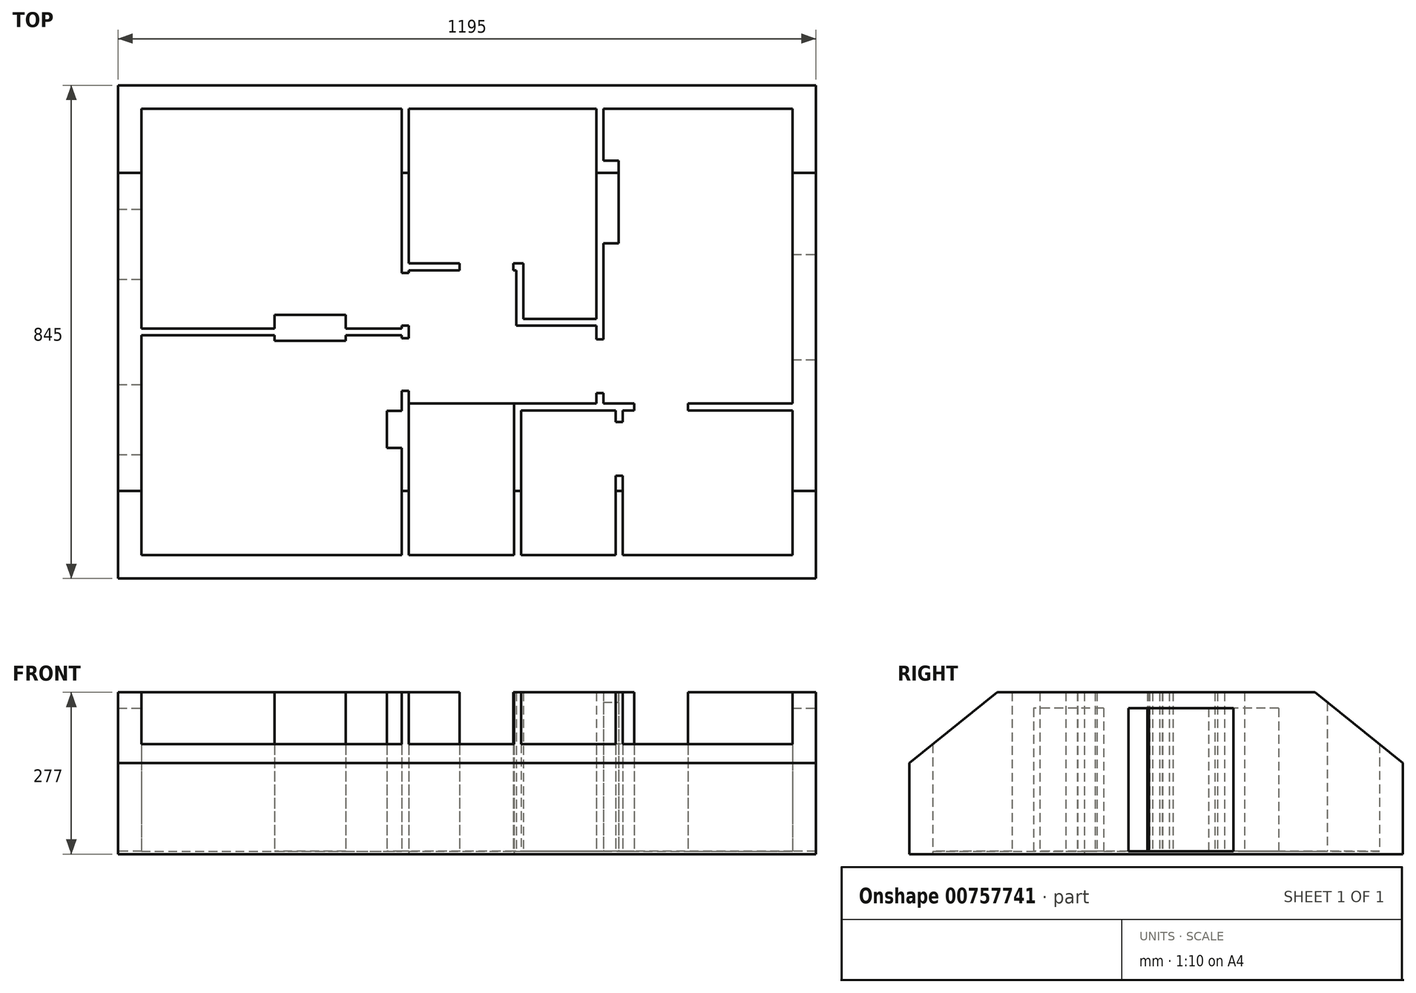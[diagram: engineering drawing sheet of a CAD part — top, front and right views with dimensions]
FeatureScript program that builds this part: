
annotation { "Feature Type Name" : "Feature", "Feature Type Description" : "" }
export const myFeature = defineFeature(function(context is Context, id is Id, definition is map)
    precondition{}
    {
        {
            var Q0;
            Q0=qCreatedBy(makeId("Top.planeOp"),FACE);
            var sketch = newSketch(context, id + "F0", { "sketchPlane" : qUnion([Q0])});
            skLineSegment(sketch, "E0", {"start": v(0, 0) * mm, "end": v(1145, 0) * mm, "construction": true});
            skLineSegment(sketch, "E1", {"start": v(1145, 0) * mm, "end": v(1145, 795) * mm, "construction": true});
            skLineSegment(sketch, "E2", {"start": v(1145, 795) * mm, "end": v(0, 795) * mm, "construction": true});
            skLineSegment(sketch, "E3", {"start": v(0, 795) * mm, "end": v(0, 0) * mm, "construction": true});
            skLineSegment(sketch, "E4", {"start": v(800, 0) * mm, "end": v(800, 15) * mm, "construction": true});
            skLineSegment(sketch, "E5", {"start": v(800, 397.5) * mm, "end": v(0, 397.5) * mm, "construction": true});
            skLineSegment(sketch, "E6.0", {"start": v(1170, 820) * mm, "end": v(-25, 820) * mm});
            skLineSegment(sketch, "E6.1", {"start": v(1170, -25) * mm, "end": v(1170, 820) * mm});
            skLineSegment(sketch, "E6.2", {"start": v(-25, -25) * mm, "end": v(1170, -25) * mm});
            skLineSegment(sketch, "E6.3", {"start": v(-25, 820) * mm, "end": v(-25, -25) * mm});
            skLineSegment(sketch, "E7.0", {"start": v(1130, 780) * mm, "end": v(15, 780) * mm});
            skLineSegment(sketch, "E7.1", {"start": v(1130, 15) * mm, "end": v(1130, 780) * mm});
            skLineSegment(sketch, "E7.2", {"start": v(15, 15) * mm, "end": v(1130, 15) * mm});
            skLineSegment(sketch, "E7.3", {"start": v(15, 780) * mm, "end": v(15, 15) * mm});
            skLineSegment(sketch, "E8.0", {"start": v(806, 263) * mm, "end": v(806, 795) * mm});
            skLineSegment(sketch, "E9.0", {"start": v(794, 263) * mm, "end": v(794, 795) * mm});
            skLineSegment(sketch, "E10", {"start": v(461, 386.5) * mm, "end": v(461, 262.5) * mm});
            skLineSegment(sketch, "E11", {"start": v(461, 262.5) * mm, "end": v(435, 262.5) * mm});
            skLineSegment(sketch, "E12", {"start": v(435, 262.5) * mm, "end": v(435, 198.5) * mm});
            skLineSegment(sketch, "E13", {"start": v(435, 198.5) * mm, "end": v(461, 198.5) * mm});
            skLineSegment(sketch, "E14", {"start": v(461, 198.5) * mm, "end": v(461, 15) * mm});
            skLineSegment(sketch, "E15", {"start": v(806, 691) * mm, "end": v(832, 691) * mm});
            skLineSegment(sketch, "E16", {"start": v(832, 691) * mm, "end": v(832, 549) * mm});
            skLineSegment(sketch, "E17", {"start": v(832, 549) * mm, "end": v(806, 549) * mm});
            skLineSegment(sketch, "E18", {"start": v(365, 426.5) * mm, "end": v(243, 426.5) * mm});
            skLineSegment(sketch, "E19", {"start": v(323, 15) * mm, "end": v(323, -25) * mm});
            skLineSegment(sketch, "E20", {"start": v(461, 15) * mm, "end": v(461, -25) * mm});
            skLineSegment(sketch, "E21", {"start": v(1130, 530) * mm, "end": v(1170, 530) * mm});
            skLineSegment(sketch, "E22", {"start": v(1130, 350) * mm, "end": v(1170, 350) * mm});
            skPoint(sketch, "E23.orphan", {"position": v(238, -25) * mm});
            skPoint(sketch, "E24.end.orphan", {"position": v(88, -25) * mm});
            skLineSegment(sketch, "E25", {"start": v(-25, 487.5) * mm, "end": v(15, 487.5) * mm});
            skLineSegment(sketch, "E26", {"start": v(-25, 607.5) * mm, "end": v(15, 607.5) * mm});
            skLineSegment(sketch, "E27", {"start": v(-25, 307.5) * mm, "end": v(15, 307.5) * mm});
            skLineSegment(sketch, "E28", {"start": v(-25, 187.5) * mm, "end": v(15, 187.5) * mm});
            skLineSegment(sketch, "E29", {"start": v(794, 408) * mm, "end": v(657, 408) * mm});
            skLineSegment(sketch, "E30", {"start": v(657, 408) * mm, "end": v(657, 503) * mm});
            skLineSegment(sketch, "E31", {"start": v(657, 503) * mm, "end": v(473, 503) * mm});
            skLineSegment(sketch, "E32.0", {"start": v(669, 515) * mm, "end": v(473, 515) * mm});
            skLineSegment(sketch, "E32.1", {"start": v(669, 420) * mm, "end": v(669, 515) * mm});
            skLineSegment(sketch, "E32.2", {"start": v(794, 420) * mm, "end": v(669, 420) * mm});
            skLineSegment(sketch, "E33", {"start": v(652, 515) * mm, "end": v(652, 503) * mm});
            skLineSegment(sketch, "E34", {"start": v(560, 515) * mm, "end": v(560, 503) * mm});
            skLineSegment(sketch, "E35", {"start": v(461, 403.5) * mm, "end": v(365, 403.5) * mm});
            skLineSegment(sketch, "E36", {"start": v(365, 403.5) * mm, "end": v(15, 403.5) * mm});
            skLineSegment(sketch, "E37", {"start": v(15, 403.5) * mm, "end": v(15, 382.16) * mm});
            skLineSegment(sketch, "E38", {"start": v(794, 385) * mm, "end": v(806, 385) * mm});
            skLineSegment(sketch, "E39", {"start": v(806, 385) * mm, "end": v(806, 293) * mm});
            skLineSegment(sketch, "E40", {"start": v(806, 293) * mm, "end": v(794, 293) * mm});
            skLineSegment(sketch, "E41.MirrorCS", {"start": v(461, 391.5) * mm, "end": v(365, 391.5) * mm});
            skLineSegment(sketch, "E42.MirrorCS", {"start": v(365, 391.5) * mm, "end": v(15, 391.5) * mm});
            skLineSegment(sketch, "E43", {"start": v(461, 403.5) * mm, "end": v(461, 408.5) * mm});
            skLineSegment(sketch, "E44", {"start": v(461, 408.5) * mm, "end": v(473, 408.5) * mm});
            skLineSegment(sketch, "E45", {"start": v(473, 408.5) * mm, "end": v(473, 386.5) * mm});
            skLineSegment(sketch, "E46", {"start": v(473, 386.5) * mm, "end": v(461, 386.5) * mm});
            skLineSegment(sketch, "E47", {"start": v(461, 386.5) * mm, "end": v(461, 391.5) * mm});
            skLineSegment(sketch, "E48", {"start": v(243, 426.5) * mm, "end": v(243, 382.5) * mm});
            skLineSegment(sketch, "E49", {"start": v(243, 382.5) * mm, "end": v(364.87, 382.5) * mm});
            skLineSegment(sketch, "E50", {"start": v(364.87, 382.5) * mm, "end": v(365, 426.5) * mm});
            skLineSegment(sketch, "E51", {"start": v(461, 408.5) * mm, "end": v(461, 780) * mm});
            skLineSegment(sketch, "E52", {"start": v(461, 780) * mm, "end": v(473, 780) * mm});
            skLineSegment(sketch, "E53", {"start": v(473, 780) * mm, "end": v(473, 408.5) * mm});
            skLineSegment(sketch, "E54", {"start": v(461, 498.5) * mm, "end": v(473, 498.5) * mm});
            skLineSegment(sketch, "E55", {"start": v(473, 386.5) * mm, "end": v(473, 15) * mm});
            skLineSegment(sketch, "E56", {"start": v(461, 296.5) * mm, "end": v(473, 296.5) * mm});
            skLineSegment(sketch, "E57", {"start": v(653, 15) * mm, "end": v(653, 275) * mm});
            skLineSegment(sketch, "E58", {"start": v(653, 275) * mm, "end": v(670, 275) * mm});
            skLineSegment(sketch, "E59", {"start": v(665, 263) * mm, "end": v(665, 15) * mm});
            skLineSegment(sketch, "E60", {"start": v(653, 275) * mm, "end": v(473, 275) * mm});
            skLineSegment(sketch, "E61", {"start": v(670, 275) * mm, "end": v(794, 275) * mm});
            skLineSegment(sketch, "E62", {"start": v(794, 275) * mm, "end": v(794, 263) * mm});
            skLineSegment(sketch, "E63", {"start": v(665, 263) * mm, "end": v(794, 263) * mm});
            skLineSegment(sketch, "E64", {"start": v(794, 275) * mm, "end": v(839, 275) * mm});
            skLineSegment(sketch, "E65", {"start": v(839, 275) * mm, "end": v(839, 15) * mm});
            skLineSegment(sketch, "E66", {"start": v(839, 15) * mm, "end": v(827, 15) * mm});
            skLineSegment(sketch, "E67", {"start": v(827, 15) * mm, "end": v(827, 263) * mm});
            skLineSegment(sketch, "E68", {"start": v(827, 263) * mm, "end": v(794, 263) * mm});
            skLineSegment(sketch, "E69", {"start": v(839, 275) * mm, "end": v(1130, 275) * mm});
            skLineSegment(sketch, "E70", {"start": v(1130, 275) * mm, "end": v(1130, 263) * mm});
            skLineSegment(sketch, "E71", {"start": v(1130, 263) * mm, "end": v(827, 263) * mm});
            skLineSegment(sketch, "E72.trimOffspring", {"start": v(800, 263) * mm, "end": v(800, 795) * mm, "construction": true});
            skLineSegment(sketch, "E73", {"start": v(827, 243) * mm, "end": v(839, 243) * mm});
            skLineSegment(sketch, "E74", {"start": v(839, 243) * mm, "end": v(839, 151) * mm});
            skLineSegment(sketch, "E75", {"start": v(839, 151) * mm, "end": v(827, 151) * mm});
            skLineSegment(sketch, "E76", {"start": v(859, 275) * mm, "end": v(859, 263) * mm});
            skLineSegment(sketch, "E77", {"start": v(859, 263) * mm, "end": v(951, 263) * mm});
            skLineSegment(sketch, "E78", {"start": v(951, 263) * mm, "end": v(951, 275) * mm});
            skSolve(sketch);
        }
        {
            var Q0;
            {var subQ5=sQuery(id+"F0.wireOp",EDGE,"E78");Q0=makeQuery(id+"F0.imprint","IMPRINT",FACE,{"disambiguationData":[TD([[makeQuery(id+"F0.imprint","IMPRINT",EDGE,{"derivedFrom":subQ5}),-1.0]])]});}
            var Q1;
            {var subQ3=sQuery(id+"F0.wireOp",EDGE,"E29");Q1=makeQuery(id+"F0.imprint","IMPRINT",FACE,{"disambiguationData":[TD([[makeQuery(id+"F0.imprint","IMPRINT",EDGE,{"derivedFrom":subQ3}),-1.0]])]});}
            var Q2;
            {var subQ2=sQuery(id+"F0.wireOp",EDGE,"E19");Q2=makeQuery(id+"F0.imprint","IMPRINT",FACE,{"disambiguationData":[TD([[makeQuery(id+"F0.imprint","IMPRINT",EDGE,{"derivedFrom":subQ2}),1.0]])]});}
            var Q3;
            {var subQ0=sQuery(id+"F0.wireOp",EDGE,"E15");Q3=makeQuery(id+"F0.imprint","IMPRINT",FACE,{"disambiguationData":[TD([[makeQuery(id+"F0.imprint","IMPRINT",EDGE,{"derivedFrom":subQ0}),1.0]])]});}
            var Q4;
            {var subQ0=sQuery(id+"F0.wireOp",EDGE,"E25");Q4=makeQuery(id+"F0.imprint","IMPRINT",FACE,{"disambiguationData":[TD([[makeQuery(id+"F0.imprint","IMPRINT",EDGE,{"derivedFrom":subQ0}),1.0]])]});}
            var Q5;
            {var subQ0=sQuery(id+"F0.wireOp",EDGE,"E27");Q5=makeQuery(id+"F0.imprint","IMPRINT",FACE,{"disambiguationData":[TD([[makeQuery(id+"F0.imprint","IMPRINT",EDGE,{"derivedFrom":subQ0}),-1.0]])]});}
            var Q6;
            {var subQ5=sQuery(id+"F0.wireOp",EDGE,"E25");Q6=makeQuery(id+"F0.imprint","IMPRINT",FACE,{"disambiguationData":[TD([[makeQuery(id+"F0.imprint","IMPRINT",EDGE,{"derivedFrom":subQ5}),-1.0]])]});}
            var Q7;
            {var subQ4=sQuery(id+"F0.wireOp",EDGE,"E19");Q7=makeQuery(id+"F0.imprint","IMPRINT",FACE,{"disambiguationData":[TD([[makeQuery(id+"F0.imprint","IMPRINT",EDGE,{"derivedFrom":subQ4}),-1.0]])]});}
            var Q8;
            {var subQ4=sQuery(id+"F0.wireOp",EDGE,"E7.1");var subQ7=sQuery(id+"F0.wireOp",EDGE,"E71");var subQ8=makeQuery(id+"F0.imprint","INTERSECT",VERTEX,{"derivedFrom":[subQ4,subQ7]});Q8=makeQuery(id+"F0.imprint","IMPRINT",FACE,{"disambiguationData":[TD([[makeQuery(id+"F0.imprint","IMPRINT",EDGE,{"disambiguationData":[TD([[subQ8,1.0]])],"derivedFrom":subQ4}),1.0]])]});}
            var Q9;
            {var subQ2=sQuery(id+"F0.wireOp",EDGE,"E76");Q9=makeQuery(id+"F0.imprint","IMPRINT",FACE,{"disambiguationData":[TD([[makeQuery(id+"F0.imprint","IMPRINT",EDGE,{"derivedFrom":subQ2}),1.0]])]});}
            var Q10;
            {var subQ5=sQuery(id+"F0.wireOp",EDGE,"E49");Q10=makeQuery(id+"F0.imprint","IMPRINT",FACE,{"disambiguationData":[TD([[makeQuery(id+"F0.imprint","IMPRINT",EDGE,{"derivedFrom":subQ5}),1.0]])]});}
            var Q11;
            {var subQ6=sQuery(id+"F0.wireOp",EDGE,"E54");Q11=makeQuery(id+"F0.imprint","IMPRINT",FACE,{"disambiguationData":[TD([[makeQuery(id+"F0.imprint","IMPRINT",EDGE,{"derivedFrom":subQ6}),1.0]])]});}
            var Q12;
            {var subQ0=sQuery(id+"F0.wireOp",EDGE,"E44");Q12=makeQuery(id+"F0.imprint","IMPRINT",FACE,{"disambiguationData":[TD([[makeQuery(id+"F0.imprint","IMPRINT",EDGE,{"derivedFrom":subQ0}),1.0]])]});}
            var Q13;
            {var subQ0=sQuery(id+"F0.wireOp",EDGE,"E18");Q13=makeQuery(id+"F0.imprint","IMPRINT",FACE,{"disambiguationData":[TD([[makeQuery(id+"F0.imprint","IMPRINT",EDGE,{"derivedFrom":subQ0}),1.0]])]});}
            var Q14;
            {var subQ9=sQuery(id+"F0.wireOp",EDGE,"E29");Q14=makeQuery(id+"F0.imprint","IMPRINT",FACE,{"disambiguationData":[TD([[makeQuery(id+"F0.imprint","IMPRINT",EDGE,{"derivedFrom":subQ9}),1.0]])]});}
            var Q15;
            {var subQ0=sQuery(id+"F0.wireOp",EDGE,"E21");Q15=makeQuery(id+"F0.imprint","IMPRINT",FACE,{"disambiguationData":[TD([[makeQuery(id+"F0.imprint","IMPRINT",EDGE,{"derivedFrom":subQ0}),-1.0]])]});}
            var Q16;
            {var subQ7=sQuery(id+"F0.wireOp",EDGE,"E59");Q16=makeQuery(id+"F0.imprint","IMPRINT",FACE,{"disambiguationData":[TD([[makeQuery(id+"F0.imprint","IMPRINT",EDGE,{"derivedFrom":subQ7}),1.0]])]});}
            var Q17;
            {var subQ0=sQuery(id+"F0.wireOp",EDGE,"E34");Q17=makeQuery(id+"F0.imprint","IMPRINT",FACE,{"disambiguationData":[TD([[makeQuery(id+"F0.imprint","IMPRINT",EDGE,{"derivedFrom":subQ0}),-1.0]])]});}
            var Q18;
            {var subQ0=sQuery(id+"F0.wireOp",EDGE,"E46");Q18=makeQuery(id+"F0.imprint","IMPRINT",FACE,{"disambiguationData":[TD([[makeQuery(id+"F0.imprint","IMPRINT",EDGE,{"derivedFrom":subQ0}),1.0]])]});}
            var Q19;
            {var subQ0=sQuery(id+"F0.wireOp",EDGE,"E11");Q19=makeQuery(id+"F0.imprint","IMPRINT",FACE,{"disambiguationData":[TD([[makeQuery(id+"F0.imprint","IMPRINT",EDGE,{"derivedFrom":subQ0}),-1.0]])]});}
            var Q20;
            {var subQ5=sQuery(id+"F0.wireOp",EDGE,"E6.0");Q20=makeQuery(id+"F0.imprint","IMPRINT",FACE,{"disambiguationData":[TD([[makeQuery(id+"F0.imprint","IMPRINT",EDGE,{"derivedFrom":subQ5}),1.0]])]});}
            var Q21;
            {var subQ2=sQuery(id+"F0.wireOp",EDGE,"E73");Q21=makeQuery(id+"F0.imprint","IMPRINT",FACE,{"disambiguationData":[TD([[makeQuery(id+"F0.imprint","IMPRINT",EDGE,{"derivedFrom":subQ2}),-1.0]])]});}
            var Q22;
            {var subQ0=sQuery(id+"F0.wireOp",EDGE,"E11");Q22=makeQuery(id+"F0.imprint","IMPRINT",FACE,{"disambiguationData":[TD([[makeQuery(id+"F0.imprint","IMPRINT",EDGE,{"derivedFrom":subQ0}),1.0]])]});}
            var Q23;
            {var subQ10=sQuery(id+"F0.wireOp",EDGE,"E32.1");Q23=makeQuery(id+"F0.imprint","IMPRINT",FACE,{"disambiguationData":[TD([[makeQuery(id+"F0.imprint","IMPRINT",EDGE,{"derivedFrom":subQ10}),-1.0]])]});}
            var Q24;
            {var subQ0=sQuery(id+"F0.wireOp",EDGE,"E15");Q24=makeQuery(id+"F0.imprint","IMPRINT",FACE,{"disambiguationData":[TD([[makeQuery(id+"F0.imprint","IMPRINT",EDGE,{"derivedFrom":subQ0}),-1.0]])]});}
            var Q25;
            {var subQ0=sQuery(id+"F0.wireOp",EDGE,"E33");Q25=makeQuery(id+"F0.imprint","IMPRINT",FACE,{"disambiguationData":[TD([[makeQuery(id+"F0.imprint","IMPRINT",EDGE,{"derivedFrom":subQ0}),-1.0]])]});}
            var Q26;
            {var subQ5=sQuery(id+"F0.wireOp",EDGE,"E75");Q26=makeQuery(id+"F0.imprint","IMPRINT",FACE,{"disambiguationData":[TD([[makeQuery(id+"F0.imprint","IMPRINT",EDGE,{"derivedFrom":subQ5}),1.0]])]});}
            var Q27;
            {var subQ3=sQuery(id+"F0.wireOp",EDGE,"E57");Q27=makeQuery(id+"F0.imprint","IMPRINT",FACE,{"disambiguationData":[TD([[makeQuery(id+"F0.imprint","IMPRINT",EDGE,{"derivedFrom":subQ3}),-1.0]])]});}
            var Q28;
            {var subQ8=sQuery(id+"F0.wireOp",EDGE,"E20");Q28=makeQuery(id+"F0.imprint","IMPRINT",FACE,{"disambiguationData":[TD([[makeQuery(id+"F0.imprint","IMPRINT",EDGE,{"derivedFrom":subQ8}),1.0]])]});}
            var Q29;
            {var subQ0=sQuery(id+"F0.wireOp",EDGE,"E38");Q29=makeQuery(id+"F0.imprint","IMPRINT",FACE,{"disambiguationData":[TD([[makeQuery(id+"F0.imprint","IMPRINT",EDGE,{"derivedFrom":subQ0}),-1.0]])]});}
            var Q30;
            {var subQ0=sQuery(id+"F0.wireOp",EDGE,"E36");var subQ1=sQuery(id+"F0.wireOp",EDGE,"E7.3");var subQ2=makeQuery(id+"F0.imprint","INTERSECT",VERTEX,{"derivedFrom":[subQ1,subQ0]});Q30=makeQuery(id+"F0.imprint","IMPRINT",FACE,{"disambiguationData":[TD([[makeQuery(id+"F0.imprint","IMPRINT",EDGE,{"disambiguationData":[TD([[subQ2,-1.0]])],"derivedFrom":subQ1}),1.0]])]});}
            var Q31;
            {var subQ3=sQuery(id+"F0.wireOp",EDGE,"E40");Q31=makeQuery(id+"F0.imprint","IMPRINT",FACE,{"disambiguationData":[TD([[makeQuery(id+"F0.imprint","IMPRINT",EDGE,{"derivedFrom":subQ3}),1.0]])]});}
            var Q32;
            {var subQ5=sQuery(id+"F0.wireOp",EDGE,"E38");Q32=makeQuery(id+"F0.imprint","IMPRINT",FACE,{"disambiguationData":[TD([[makeQuery(id+"F0.imprint","IMPRINT",EDGE,{"derivedFrom":subQ5}),1.0]])]});}
            var Q33;
            {var subQ3=sQuery(id+"F0.wireOp",EDGE,"E73");Q33=makeQuery(id+"F0.imprint","IMPRINT",FACE,{"disambiguationData":[TD([[makeQuery(id+"F0.imprint","IMPRINT",EDGE,{"derivedFrom":subQ3}),1.0]])]});}
            var Q34;
            {var subQ3=sQuery(id+"F0.wireOp",EDGE,"E64");var subQ5=sQuery(id+"F0.wireOp",EDGE,"E8.0");var subQ6=makeQuery(id+"F0.imprint","INTERSECT",VERTEX,{"derivedFrom":[subQ5,subQ3]});Q34=makeQuery(id+"F0.imprint","IMPRINT",FACE,{"disambiguationData":[TD([[makeQuery(id+"F0.imprint","IMPRINT",EDGE,{"disambiguationData":[TD([[subQ6,1.0]])],"derivedFrom":subQ5}),-1.0]])]});}
            var Q35;
            {var subQ5=sQuery(id+"F0.wireOp",EDGE,"E76");Q35=makeQuery(id+"F0.imprint","IMPRINT",FACE,{"disambiguationData":[TD([[makeQuery(id+"F0.imprint","IMPRINT",EDGE,{"derivedFrom":subQ5}),-1.0]])]});}
            var Q36;
            {var subQ6=sQuery(id+"F0.wireOp",EDGE,"E35");Q36=makeQuery(id+"F0.imprint","IMPRINT",FACE,{"disambiguationData":[TD([[makeQuery(id+"F0.imprint","IMPRINT",EDGE,{"derivedFrom":subQ6}),1.0]])]});}
            var Q37;
            {var subQ0=sQuery(id+"F0.wireOp",EDGE,"E48");var subQ1=sQuery(id+"F0.wireOp",EDGE,"E36");var subQ2=makeQuery(id+"F0.imprint","INTERSECT",VERTEX,{"derivedFrom":[subQ1,subQ0]});Q37=makeQuery(id+"F0.imprint","IMPRINT",FACE,{"disambiguationData":[TD([[makeQuery(id+"F0.imprint","IMPRINT",EDGE,{"disambiguationData":[TD([[subQ2,1.0]])],"derivedFrom":subQ1}),1.0]])]});}
            var Q38;
            {var subQ0=sQuery(id+"F0.wireOp",EDGE,"E64");var subQ1=sQuery(id+"F0.wireOp",EDGE,"E8.0");var subQ2=makeQuery(id+"F0.imprint","INTERSECT",VERTEX,{"derivedFrom":[subQ1,subQ0]});Q38=makeQuery(id+"F0.imprint","IMPRINT",FACE,{"disambiguationData":[TD([[makeQuery(id+"F0.imprint","IMPRINT",EDGE,{"disambiguationData":[TD([[subQ2,1.0]])],"derivedFrom":subQ1}),1.0]])]});}
            var Q39;
            {var subQ1=sQuery(id+"F0.wireOp",EDGE,"E18");Q39=makeQuery(id+"F0.imprint","IMPRINT",FACE,{"disambiguationData":[TD([[makeQuery(id+"F0.imprint","IMPRINT",EDGE,{"derivedFrom":subQ1}),-1.0]])]});}
            extrude(context, id + "F1", {"entities" : qUnion([Q0, Q1, Q2, Q3, Q4, Q5, Q6, Q7, Q8, Q9, Q10, Q11, Q12, Q13, Q14, Q15, Q16, Q17, Q18, Q19, Q20, Q21, Q22, Q23, Q24, Q25, Q26, Q27, Q28, Q29, Q30, Q31, Q32, Q33, Q34, Q35, Q36, Q37, Q38, Q39]), "depth" : 5 * mm, "offsetDistance" : 25 * mm});
        }
        {
            var Q0;
            {var subQ4=sQuery(id+"F0.wireOp",EDGE,"E19");Q0=makeQuery(id+"F0.imprint","IMPRINT",FACE,{"disambiguationData":[TD([[makeQuery(id+"F0.imprint","IMPRINT",EDGE,{"derivedFrom":subQ4}),-1.0]])]});}
            var Q1;
            {var subQ2=sQuery(id+"F0.wireOp",EDGE,"E19");Q1=makeQuery(id+"F0.imprint","IMPRINT",FACE,{"disambiguationData":[TD([[makeQuery(id+"F0.imprint","IMPRINT",EDGE,{"derivedFrom":subQ2}),1.0]])]});}
            var Q2;
            {var subQ8=sQuery(id+"F0.wireOp",EDGE,"E20");Q2=makeQuery(id+"F0.imprint","IMPRINT",FACE,{"disambiguationData":[TD([[makeQuery(id+"F0.imprint","IMPRINT",EDGE,{"derivedFrom":subQ8}),1.0]])]});}
            var Q3;
            {var subQ5=sQuery(id+"F0.wireOp",EDGE,"E75");Q3=makeQuery(id+"F0.imprint","IMPRINT",FACE,{"disambiguationData":[TD([[makeQuery(id+"F0.imprint","IMPRINT",EDGE,{"derivedFrom":subQ5}),1.0]])]});}
            var Q4;
            {var subQ3=sQuery(id+"F0.wireOp",EDGE,"E57");Q4=makeQuery(id+"F0.imprint","IMPRINT",FACE,{"disambiguationData":[TD([[makeQuery(id+"F0.imprint","IMPRINT",EDGE,{"derivedFrom":subQ3}),-1.0]])]});}
            var Q5;
            {var subQ0=sQuery(id+"F0.wireOp",EDGE,"E11");Q5=makeQuery(id+"F0.imprint","IMPRINT",FACE,{"disambiguationData":[TD([[makeQuery(id+"F0.imprint","IMPRINT",EDGE,{"derivedFrom":subQ0}),1.0]])]});}
            var Q6;
            {var subQ5=sQuery(id+"F0.wireOp",EDGE,"E25");Q6=makeQuery(id+"F0.imprint","IMPRINT",FACE,{"disambiguationData":[TD([[makeQuery(id+"F0.imprint","IMPRINT",EDGE,{"derivedFrom":subQ5}),-1.0]])]});}
            var Q7;
            {var subQ0=sQuery(id+"F0.wireOp",EDGE,"E36");var subQ1=sQuery(id+"F0.wireOp",EDGE,"E7.3");var subQ2=makeQuery(id+"F0.imprint","INTERSECT",VERTEX,{"derivedFrom":[subQ1,subQ0]});Q7=makeQuery(id+"F0.imprint","IMPRINT",FACE,{"disambiguationData":[TD([[makeQuery(id+"F0.imprint","IMPRINT",EDGE,{"disambiguationData":[TD([[subQ2,-1.0]])],"derivedFrom":subQ1}),1.0]])]});}
            var Q8;
            {var subQ0=sQuery(id+"F0.wireOp",EDGE,"E18");Q8=makeQuery(id+"F0.imprint","IMPRINT",FACE,{"disambiguationData":[TD([[makeQuery(id+"F0.imprint","IMPRINT",EDGE,{"derivedFrom":subQ0}),1.0]])]});}
            var Q9;
            {var subQ0=sQuery(id+"F0.wireOp",EDGE,"E48");var subQ1=sQuery(id+"F0.wireOp",EDGE,"E36");var subQ2=makeQuery(id+"F0.imprint","INTERSECT",VERTEX,{"derivedFrom":[subQ1,subQ0]});Q9=makeQuery(id+"F0.imprint","IMPRINT",FACE,{"disambiguationData":[TD([[makeQuery(id+"F0.imprint","IMPRINT",EDGE,{"disambiguationData":[TD([[subQ2,1.0]])],"derivedFrom":subQ1}),1.0]])]});}
            var Q10;
            {var subQ5=sQuery(id+"F0.wireOp",EDGE,"E49");Q10=makeQuery(id+"F0.imprint","IMPRINT",FACE,{"disambiguationData":[TD([[makeQuery(id+"F0.imprint","IMPRINT",EDGE,{"derivedFrom":subQ5}),1.0]])]});}
            var Q11;
            {var subQ6=sQuery(id+"F0.wireOp",EDGE,"E35");Q11=makeQuery(id+"F0.imprint","IMPRINT",FACE,{"disambiguationData":[TD([[makeQuery(id+"F0.imprint","IMPRINT",EDGE,{"derivedFrom":subQ6}),1.0]])]});}
            var Q12;
            {var subQ6=sQuery(id+"F0.wireOp",EDGE,"E54");Q12=makeQuery(id+"F0.imprint","IMPRINT",FACE,{"disambiguationData":[TD([[makeQuery(id+"F0.imprint","IMPRINT",EDGE,{"derivedFrom":subQ6}),1.0]])]});}
            var Q13;
            {var subQ0=sQuery(id+"F0.wireOp",EDGE,"E34");Q13=makeQuery(id+"F0.imprint","IMPRINT",FACE,{"disambiguationData":[TD([[makeQuery(id+"F0.imprint","IMPRINT",EDGE,{"derivedFrom":subQ0}),-1.0]])]});}
            var Q14;
            {var subQ3=sQuery(id+"F0.wireOp",EDGE,"E29");Q14=makeQuery(id+"F0.imprint","IMPRINT",FACE,{"disambiguationData":[TD([[makeQuery(id+"F0.imprint","IMPRINT",EDGE,{"derivedFrom":subQ3}),-1.0]])]});}
            var Q15;
            {var subQ5=sQuery(id+"F0.wireOp",EDGE,"E38");Q15=makeQuery(id+"F0.imprint","IMPRINT",FACE,{"disambiguationData":[TD([[makeQuery(id+"F0.imprint","IMPRINT",EDGE,{"derivedFrom":subQ5}),1.0]])]});}
            var Q16;
            {var subQ3=sQuery(id+"F0.wireOp",EDGE,"E73");Q16=makeQuery(id+"F0.imprint","IMPRINT",FACE,{"disambiguationData":[TD([[makeQuery(id+"F0.imprint","IMPRINT",EDGE,{"derivedFrom":subQ3}),1.0]])]});}
            var Q17;
            {var subQ5=sQuery(id+"F0.wireOp",EDGE,"E76");Q17=makeQuery(id+"F0.imprint","IMPRINT",FACE,{"disambiguationData":[TD([[makeQuery(id+"F0.imprint","IMPRINT",EDGE,{"derivedFrom":subQ5}),-1.0]])]});}
            var Q18;
            {var subQ3=sQuery(id+"F0.wireOp",EDGE,"E64");var subQ5=sQuery(id+"F0.wireOp",EDGE,"E8.0");var subQ6=makeQuery(id+"F0.imprint","INTERSECT",VERTEX,{"derivedFrom":[subQ5,subQ3]});Q18=makeQuery(id+"F0.imprint","IMPRINT",FACE,{"disambiguationData":[TD([[makeQuery(id+"F0.imprint","IMPRINT",EDGE,{"disambiguationData":[TD([[subQ6,1.0]])],"derivedFrom":subQ5}),-1.0]])]});}
            var Q19;
            {var subQ0=sQuery(id+"F0.wireOp",EDGE,"E64");var subQ1=sQuery(id+"F0.wireOp",EDGE,"E8.0");var subQ2=makeQuery(id+"F0.imprint","INTERSECT",VERTEX,{"derivedFrom":[subQ1,subQ0]});Q19=makeQuery(id+"F0.imprint","IMPRINT",FACE,{"disambiguationData":[TD([[makeQuery(id+"F0.imprint","IMPRINT",EDGE,{"disambiguationData":[TD([[subQ2,1.0]])],"derivedFrom":subQ1}),1.0]])]});}
            var Q20;
            {var subQ3=sQuery(id+"F0.wireOp",EDGE,"E40");Q20=makeQuery(id+"F0.imprint","IMPRINT",FACE,{"disambiguationData":[TD([[makeQuery(id+"F0.imprint","IMPRINT",EDGE,{"derivedFrom":subQ3}),1.0]])]});}
            var Q21;
            {var subQ5=sQuery(id+"F0.wireOp",EDGE,"E78");Q21=makeQuery(id+"F0.imprint","IMPRINT",FACE,{"disambiguationData":[TD([[makeQuery(id+"F0.imprint","IMPRINT",EDGE,{"derivedFrom":subQ5}),-1.0]])]});}
            var Q22;
            {var subQ5=sQuery(id+"F0.wireOp",EDGE,"E6.0");Q22=makeQuery(id+"F0.imprint","IMPRINT",FACE,{"disambiguationData":[TD([[makeQuery(id+"F0.imprint","IMPRINT",EDGE,{"derivedFrom":subQ5}),1.0]])]});}
            var Q23;
            {var subQ0=sQuery(id+"F0.wireOp",EDGE,"E15");Q23=makeQuery(id+"F0.imprint","IMPRINT",FACE,{"disambiguationData":[TD([[makeQuery(id+"F0.imprint","IMPRINT",EDGE,{"derivedFrom":subQ0}),-1.0]])]});}
            extrude(context, id + "F2", {"entities" : qUnion([Q0, Q1, Q2, Q3, Q4, Q5, Q6, Q7, Q8, Q9, Q10, Q11, Q12, Q13, Q14, Q15, Q16, Q17, Q18, Q19, Q20, Q21, Q22, Q23]), "operationType" : NewBodyOperationType.ADD, "depth" : (549 - 272) * mm, "offsetDistance" : 25 * mm});
        }
        {
            var Q0;
            Q0=makeQuery(id+"F2.opExtrude","CAP_FACE",FACE,{"disambiguationData":[OSD([sQuery(id+"F0.wireOp",EDGE,"E6.0"),sQuery(id+"F0.wireOp",EDGE,"E6.1"),sQuery(id+"F0.wireOp",EDGE,"E6.3"),sQuery(id+"F0.wireOp",EDGE,"E7.0"),sQuery(id+"F0.wireOp",EDGE,"E7.1"),sQuery(id+"F0.wireOp",EDGE,"E7.3"),sQuery(id+"F0.wireOp",EDGE,"E8.0"),sQuery(id+"F0.wireOp",EDGE,"E9.0"),sQuery(id+"F0.wireOp",EDGE,"E15"),sQuery(id+"F0.wireOp",EDGE,"E16"),sQuery(id+"F0.wireOp",EDGE,"E17"),sQuery(id+"F0.wireOp",EDGE,"E21"),sQuery(id+"F0.wireOp",EDGE,"E26"),sQuery(id+"F0.wireOp",EDGE,"E29"),sQuery(id+"F0.wireOp",EDGE,"E30"),sQuery(id+"F0.wireOp",EDGE,"E31"),sQuery(id+"F0.wireOp",EDGE,"E32.0"),sQuery(id+"F0.wireOp",EDGE,"E32.1"),sQuery(id+"F0.wireOp",EDGE,"E32.2"),sQuery(id+"F0.wireOp",EDGE,"E33"),sQuery(id+"F0.wireOp",EDGE,"E34"),sQuery(id+"F0.wireOp",EDGE,"E38"),sQuery(id+"F0.wireOp",EDGE,"E51"),sQuery(id+"F0.wireOp",EDGE,"E53"),sQuery(id+"F0.wireOp",EDGE,"E54")])],"isStart":false});
            var sketch = newSketch(context, id + "F3", { "sketchPlane" : qUnion([Q0])});
            skLineSegment(sketch, "E79.0", {"start": v(15, 780) * mm, "end": v(15, 15) * mm});
            skLineSegment(sketch, "E80.0", {"start": v(-25, 820) * mm, "end": v(-25, -25) * mm});
            skLineSegment(sketch, "E81.0", {"start": v(-25, 487.5) * mm, "end": v(15, 487.5) * mm});
            skLineSegment(sketch, "E82.0", {"start": v(-25, 607.5) * mm, "end": v(15, 607.5) * mm});
            skLineSegment(sketch, "E83.0", {"start": v(-25, 307.5) * mm, "end": v(15, 307.5) * mm});
            skLineSegment(sketch, "E84.0", {"start": v(-25, 187.5) * mm, "end": v(15, 187.5) * mm});
            skLineSegment(sketch, "E85.0", {"start": v(1170, -25) * mm, "end": v(1170, 820) * mm});
            skLineSegment(sketch, "E86.0", {"start": v(1130, 15) * mm, "end": v(1130, 780) * mm});
            skLineSegment(sketch, "E87.0", {"start": v(1130, 530) * mm, "end": v(1170, 530) * mm});
            skLineSegment(sketch, "E88.0", {"start": v(1130, 350) * mm, "end": v(1170, 350) * mm});
            skSolve(sketch);
        }
        {
            var Q0;
            Q0 = qSketchRegion(id + "F3", true);
            extrude(context, id + "F4", {"entities" : qUnion([Q0]), "operationType" : NewBodyOperationType.ADD, "oppositeDirection" : true, "depth" : (277 - 250) * mm, "offsetDistance" : 25 * mm});
        }
        {
            var Q0;
            {var subQ0=sQuery(id+"F0.wireOp",EDGE,"E6.3");Q0=makeQuery(id+"F4.boolean.opBoolean","MERGE",FACE,{"derivedFrom":[makeQuery(id+"F2.boolean.opBoolean","MERGE",FACE,{"derivedFrom":[makeQuery(id+"F1.opExtrude","SWEPT_FACE",FACE,{"disambiguationData":[OSD([subQ0])]}),makeQuery(id+"F2.opExtrude","SWEPT_FACE",FACE,{"disambiguationData":[OSD([subQ0]),TDD([makeQuery(id+"F0.imprint","IMPRINT",EDGE,{"disambiguationData":[TD([[makeQuery(id+"F0.imprint","INTERSECT",VERTEX,{"derivedFrom":[sQuery(id+"F0.wireOp",EDGE,"E6.0"),subQ0]}),-1.0]])],"derivedFrom":subQ0})])]}),makeQuery(id+"F2.opExtrude","SWEPT_FACE",FACE,{"disambiguationData":[OSD([subQ0]),TDD([makeQuery(id+"F0.imprint","IMPRINT",EDGE,{"disambiguationData":[TD([[makeQuery(id+"F0.imprint","INTERSECT",VERTEX,{"derivedFrom":[subQ0,sQuery(id+"F0.wireOp",EDGE,"E28")]}),-1.0]])],"derivedFrom":subQ0})])]}),makeQuery(id+"F2.opExtrude","SWEPT_FACE",FACE,{"disambiguationData":[OSD([subQ0]),TDD([makeQuery(id+"F0.imprint","IMPRINT",EDGE,{"disambiguationData":[TD([[makeQuery(id+"F0.imprint","INTERSECT",VERTEX,{"derivedFrom":[subQ0,sQuery(id+"F0.wireOp",EDGE,"E25")]}),-1.0]])],"derivedFrom":subQ0})])]})]}),makeQuery(id+"F4.opExtrude","SWEPT_FACE",FACE,{"disambiguationData":[OSD([sQuery(id+"F3.wireOp",EDGE,"E80.0")])]})]});}
            var sketch = newSketch(context, id + "F5", { "sketchPlane" : qUnion([Q0])});
            skLineSegment(sketch, "E89", {"start": v(-397.5, 277) * mm, "end": v(-397.5, 496) * mm, "construction": true});
            skLineSegment(sketch, "E90", {"start": v(-820, 0) * mm, "end": v(-820, 156) * mm, "construction": true});
            skLineSegment(sketch, "E91", {"start": v(-397.5, 496) * mm, "end": v(-820, 156) * mm});
            skLineSegment(sketch, "E92.MirrorCS", {"start": v(-397.5, 496) * mm, "end": v(25, 156) * mm});
            skLineSegment(sketch, "E93", {"start": v(-820, 156) * mm, "end": v(-820, 496) * mm});
            skLineSegment(sketch, "E94", {"start": v(-820, 496) * mm, "end": v(25, 496) * mm});
            skLineSegment(sketch, "E95", {"start": v(25, 496) * mm, "end": v(25, 156) * mm});
            skSolve(sketch);
        }
        {
            var Q0;
            {var subQ0=sQuery(id+"F5.wireOp",EDGE,"E94");var subQ6=sQuery(id+"F5.wireOp",EDGE,"E93");var subQ8=makeQuery(id+"F5.imprint","INTERSECT",VERTEX,{"derivedFrom":[subQ6,subQ0]});Q0=makeQuery(id+"F5.imprint","IMPRINT",FACE,{"disambiguationData":[TD([[makeQuery(id+"F5.imprint","IMPRINT",EDGE,{"disambiguationData":[TD([[subQ8,-1.0]])],"derivedFrom":subQ0}),-1.0]])]});}
            var Q1;
            {var subQ0=sQuery(id+"F5.wireOp",EDGE,"E93");var subQ1=sQuery(id+"F5.wireOp",EDGE,"E91");var subQ2=sQuery(id+"F0.wireOp",EDGE,"E6.3");var subQ3=sQuery(id+"F0.wireOp",EDGE,"E6.0");var subQ4=makeQuery(id+"F5.imprint","INTERSECT",VERTEX,{"derivedFrom":[makeQuery(id+"F2.boolean.opBoolean","MERGE",EDGE,{"derivedFrom":[makeQuery(id+"F1.opExtrude","SWEPT_EDGE",EDGE,{"disambiguationData":[OSD([subQ3,subQ2])]}),makeQuery(id+"F2.opExtrude","SWEPT_EDGE",EDGE,{"disambiguationData":[OSD([subQ3,subQ2])]})]}),subQ1,subQ0]});Q1=makeQuery(id+"F5.imprint","IMPRINT",FACE,{"disambiguationData":[TD([[makeQuery(id+"F5.imprint","IMPRINT",EDGE,{"disambiguationData":[TD([[subQ4,1.0]])],"derivedFrom":subQ1}),-1.0]])]});}
            var Q2;
            {var subQ0=sQuery(id+"F5.wireOp",EDGE,"E94");var subQ6=sQuery(id+"F5.wireOp",EDGE,"E95");var subQ7=makeQuery(id+"F5.imprint","INTERSECT",VERTEX,{"derivedFrom":[subQ0,subQ6]});Q2=makeQuery(id+"F5.imprint","IMPRINT",FACE,{"disambiguationData":[TD([[makeQuery(id+"F5.imprint","IMPRINT",EDGE,{"disambiguationData":[TD([[subQ7,1.0]])],"derivedFrom":subQ0}),-1.0]])]});}
            var Q3;
            {var subQ0=sQuery(id+"F5.wireOp",EDGE,"E95");var subQ1=sQuery(id+"F5.wireOp",EDGE,"E92.MirrorCS");var subQ2=sQuery(id+"F0.wireOp",EDGE,"E6.3");var subQ3=sQuery(id+"F0.wireOp",EDGE,"E6.2");var subQ4=makeQuery(id+"F5.imprint","INTERSECT",VERTEX,{"derivedFrom":[makeQuery(id+"F2.boolean.opBoolean","MERGE",EDGE,{"derivedFrom":[makeQuery(id+"F1.opExtrude","SWEPT_EDGE",EDGE,{"disambiguationData":[OSD([subQ3,subQ2])]}),makeQuery(id+"F2.opExtrude","SWEPT_EDGE",EDGE,{"disambiguationData":[OSD([subQ3,subQ2])]})]}),subQ1,subQ0]});Q3=makeQuery(id+"F5.imprint","IMPRINT",FACE,{"disambiguationData":[TD([[makeQuery(id+"F5.imprint","IMPRINT",EDGE,{"disambiguationData":[TD([[subQ4,1.0]])],"derivedFrom":subQ1}),1.0]])]});}
            extrude(context, id + "F6", {"entities" : qUnion([Q0, Q1, Q2, Q3]), "operationType" : NewBodyOperationType.REMOVE, "endBound" : BoundingType.THROUGH_ALL, "oppositeDirection" : true, "depth" : 25 * mm, "offsetDistance" : 25 * mm});
        }
    });
